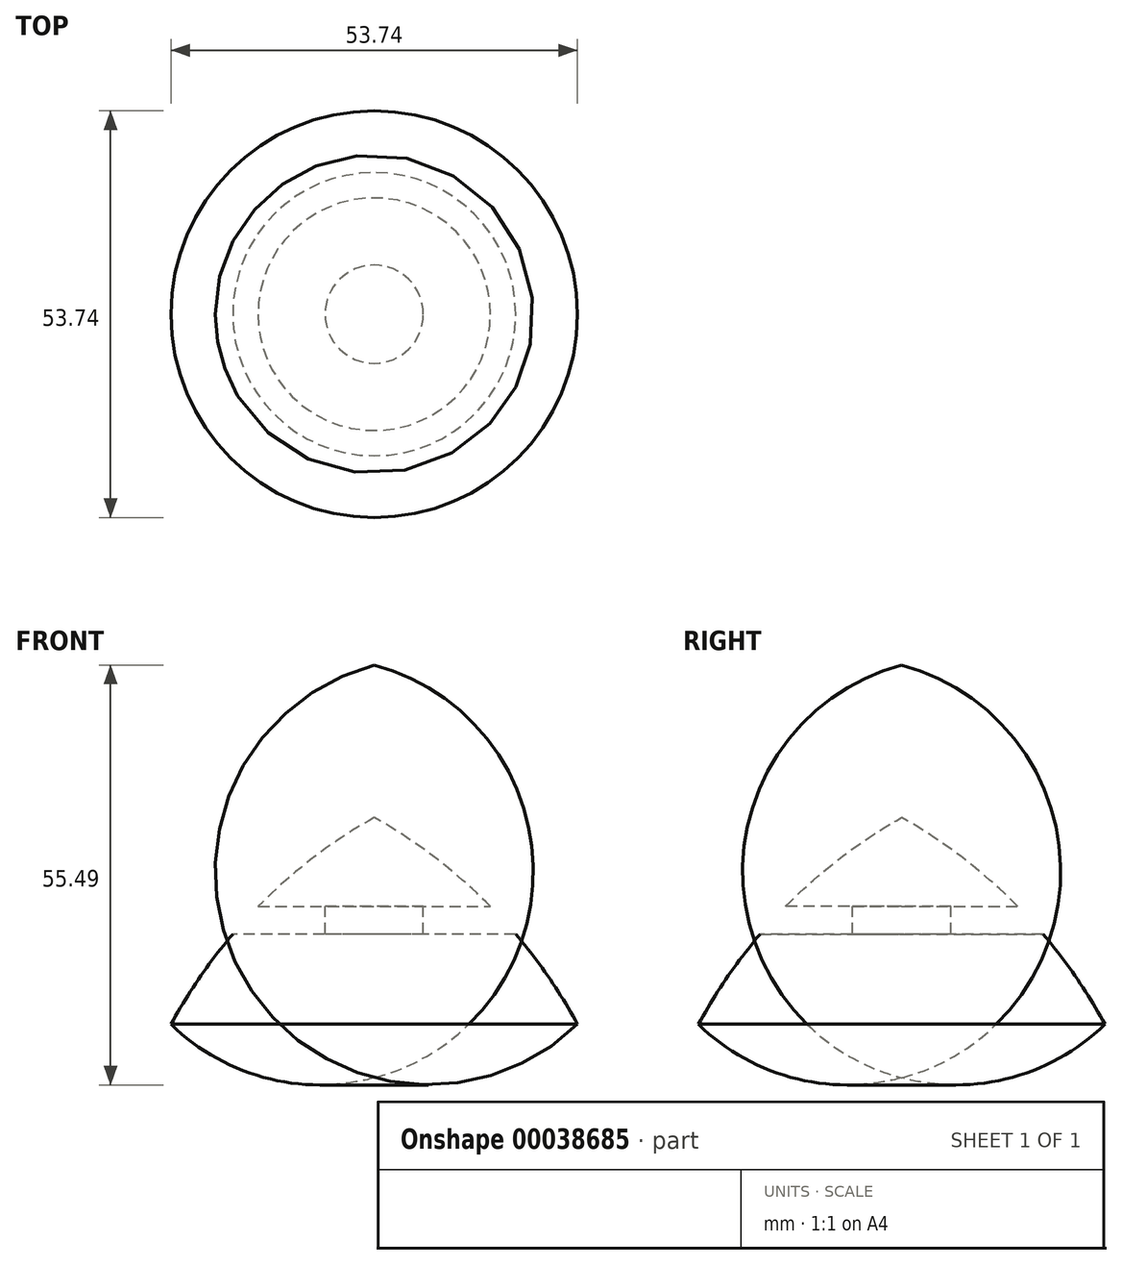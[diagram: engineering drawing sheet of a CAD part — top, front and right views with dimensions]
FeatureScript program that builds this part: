
annotation { "Feature Type Name" : "Feature", "Feature Type Description" : "" }
export const myFeature = defineFeature(function(context is Context, id is Id, definition is map)
    precondition{}
    {
        {
            var Q0;
            Q0=qCreatedBy(makeId("Right.planeOp"),FACE);
            var sketch = newSketch(context, id + "F0", { "sketchPlane" : qUnion([Q0])});
            skArc(sketch, "E0", {"start": v(0, 27.34) * mm, "mid": v(-15.36, 15.57) * mm, "end": v(-26.87, 0) * mm});
            skArc(sketch, "E1", {"start": v(-26.87, 0) * mm, "mid": v(-14.37, -7.08) * mm, "end": v(0, -7.08) * mm});
            skLineSegment(sketch, "E2", {"start": v(0, 27.34) * mm, "end": v(0, -7.08) * mm});
            skPoint(sketch, "E3.firstSnap0", {"position": v(-15.36, 15.57) * mm});
            skLineSegment(sketch, "E3.bottom", {"start": v(-22.02, 15.57) * mm, "end": v(6.49, 15.57) * mm});
            skLineSegment(sketch, "E3.top", {"start": v(-22.02, 11.91) * mm, "end": v(6.49, 11.91) * mm});
            skLineSegment(sketch, "E3.left", {"start": v(-22.02, 15.57) * mm, "end": v(-22.02, 11.91) * mm});
            skLineSegment(sketch, "E3.right", {"start": v(6.49, 15.57) * mm, "end": v(6.49, 11.91) * mm});
            skSolve(sketch);
        }
        {
            var Q0;
            {var subQ1=sQuery(id+"F0.wireOp",EDGE,"E2");var subQ3=sQuery(id+"F0.wireOp",EDGE,"E0");var subQ5=makeQuery(id+"F0.imprint","INTERSECT",VERTEX,{"derivedFrom":[subQ3,subQ1]});Q0=makeQuery(id+"F0.imprint","IMPRINT",FACE,{"disambiguationData":[TD([[makeQuery(id+"F0.imprint","IMPRINT",EDGE,{"disambiguationData":[TD([[subQ5,-1.0]])],"derivedFrom":subQ3}),1.0]])]});}
            var Q1;
            {var subQ5=sQuery(id+"F0.wireOp",EDGE,"E1");Q1=makeQuery(id+"F0.imprint","IMPRINT",FACE,{"disambiguationData":[TD([[makeQuery(id+"F0.imprint","IMPRINT",EDGE,{"derivedFrom":subQ5}),1.0]])]});}
            var Q2;
            {var subQ0=sQuery(id+"F0.wireOp",EDGE,"E3.right");Q2=makeQuery(id+"F0.imprint","IMPRINT",FACE,{"disambiguationData":[TD([[makeQuery(id+"F0.imprint","IMPRINT",EDGE,{"derivedFrom":subQ0}),-1.0]])]});}
            var Q3;
            Q3=sQuery(id+"F0.wireOp",EDGE,"E2");
            revolve(context, id + "F1", {"entities" : qUnion([Q0, Q1, Q2]), "axis" : qUnion([Q3]), "revolveType" : RevolveType.FULL});
        }
    });
